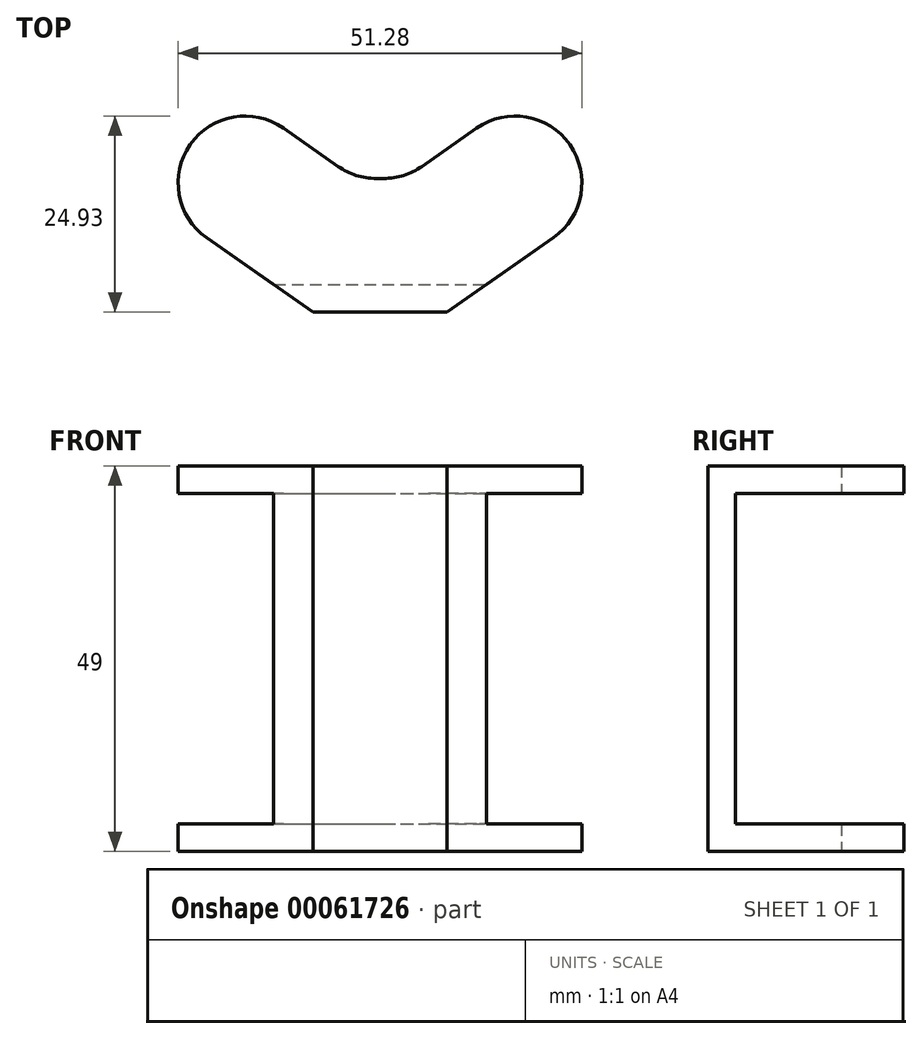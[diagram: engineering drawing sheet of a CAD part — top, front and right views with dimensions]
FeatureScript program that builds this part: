
annotation { "Feature Type Name" : "Feature", "Feature Type Description" : "" }
export const myFeature = defineFeature(function(context is Context, id is Id, definition is map)
    precondition{}
    {
        {
            var Q0;
            Q0=qCreatedBy(makeId("Top.planeOp"),FACE);
            var sketch = newSketch(context, id + "F0", { "sketchPlane" : qUnion([Q0])});
            skLineSegment(sketch, "E0", {"start": v(0, 0) * mm, "end": v(8.5, 0) * mm});
            skLineSegment(sketch, "E1", {"start": v(8.5, 0) * mm, "end": v(22.02, 9.46) * mm});
            skLineSegment(sketch, "E2", {"start": v(24.1, 21.3) * mm, "end": v(24.1, 21.3) * mm});
            skLineSegment(sketch, "E3", {"start": v(12.27, 23.39) * mm, "end": v(5.34, 18.54) * mm});
            skLineSegment(sketch, "E4", {"start": v(0.46, 17) * mm, "end": v(0, 17) * mm});
            skLineSegment(sketch, "E5", {"start": v(0, 17) * mm, "end": v(0, 0) * mm});
            skPoint(sketch, "E6.visualSharp", {"position": v(19.23, 28.26) * mm});
            skArc(sketch, "E6.filletArc", {"start": v(24.1, 21.3) * mm, "mid": v(18.62, 24.8) * mm, "end": v(12.27, 23.39) * mm});
            skPoint(sketch, "E7.visualSharp", {"position": v(28.98, 14.34) * mm});
            skArc(sketch, "E7.filletArc", {"start": v(22.02, 9.46) * mm, "mid": v(25.51, 14.95) * mm, "end": v(24.1, 21.3) * mm});
            skPoint(sketch, "E8.visualSharp", {"position": v(3.14, 17) * mm});
            skArc(sketch, "E8.filletArc", {"start": v(0.46, 17) * mm, "mid": v(3.02, 17.4) * mm, "end": v(5.34, 18.54) * mm});
            skLineSegment(sketch, "E9.MirrorCS", {"start": v(-0.46, 17) * mm, "end": v(0, 17) * mm});
            skLineSegment(sketch, "E10.MirrorCS", {"start": v(-24.1, 21.3) * mm, "end": v(-24.1, 21.3) * mm});
            skLineSegment(sketch, "E11.MirrorCS", {"start": v(0, 0) * mm, "end": v(-8.5, 0) * mm});
            skLineSegment(sketch, "E12.MirrorCS", {"start": v(-8.5, 0) * mm, "end": v(-22.02, 9.46) * mm});
            skLineSegment(sketch, "E13.MirrorCS", {"start": v(-12.27, 23.39) * mm, "end": v(-5.34, 18.54) * mm});
            skPoint(sketch, "E14.MirrorP", {"position": v(-3.14, 17) * mm});
            skPoint(sketch, "E15.MirrorP", {"position": v(-28.98, 14.34) * mm});
            skArc(sketch, "E16.MirrorCS", {"start": v(-24.1, 21.3) * mm, "mid": v(-18.62, 24.8) * mm, "end": v(-12.27, 23.39) * mm});
            skPoint(sketch, "E17.MirrorP", {"position": v(-19.23, 28.26) * mm});
            skArc(sketch, "E18.MirrorCS", {"start": v(-0.46, 17) * mm, "mid": v(-3.02, 17.4) * mm, "end": v(-5.34, 18.54) * mm});
            skArc(sketch, "E19.MirrorCS", {"start": v(-22.02, 9.46) * mm, "mid": v(-25.51, 14.95) * mm, "end": v(-24.1, 21.3) * mm});
            skSolve(sketch);
        }
        {
            assignVariable(context, id + "F1", {"name" : "height", "anyValue" : 49});
        }
        {
            var Q0;
            Q0=makeQuery(id+"F0.imprint","IMPRINT",FACE,{"disambiguationData":[TD([[makeQuery(id+"F0.imprint","IMPRINT",EDGE,{"derivedFrom":sQuery(id+"F0.wireOp",EDGE,"E5")}),-1.0]])]});
            var Q1;
            Q1=makeQuery(id+"F0.imprint","IMPRINT",FACE,{"disambiguationData":[TD([[makeQuery(id+"F0.imprint","IMPRINT",EDGE,{"derivedFrom":sQuery(id+"F0.wireOp",EDGE,"E0")}),1.0]])]});
            extrude(context, id + "F2", {"entities" : qUnion([Q0, Q1]), "depth" : (getVariable(context, 'height')) * mm});
        }
        {
            var Q0;
            Q0=qCreatedBy(makeId("Right.planeOp"),FACE);
            var sketch = newSketch(context, id + "F3", { "sketchPlane" : qUnion([Q0])});
            skLineSegment(sketch, "E20.bottom", {"start": v(71.98, 3.5) * mm, "end": v(3.5, 3.5) * mm});
            skLineSegment(sketch, "E20.top", {"start": v(71.98, 45.5) * mm, "end": v(3.5, 45.5) * mm});
            skLineSegment(sketch, "E20.left", {"start": v(71.98, 3.5) * mm, "end": v(71.98, 45.5) * mm});
            skLineSegment(sketch, "E20.right", {"start": v(3.5, 3.5) * mm, "end": v(3.5, 45.5) * mm});
            skSolve(sketch);
        }
        {
            var Q0;
            Q0=makeQuery(id+"F3.imprint","IMPRINT",FACE,{"disambiguationData":[TD([[makeQuery(id+"F3.imprint","IMPRINT",EDGE,{"derivedFrom":sQuery(id+"F3.wireOp",EDGE,"E20.bottom")}),-1.0]])]});
            extrude(context, id + "F4", {"entities" : qUnion([Q0]), "operationType" : NewBodyOperationType.REMOVE, "endBound" : BoundingType.SYMMETRIC, "oppositeDirection" : true, "depth" : 999 * mm});
        }
    });
